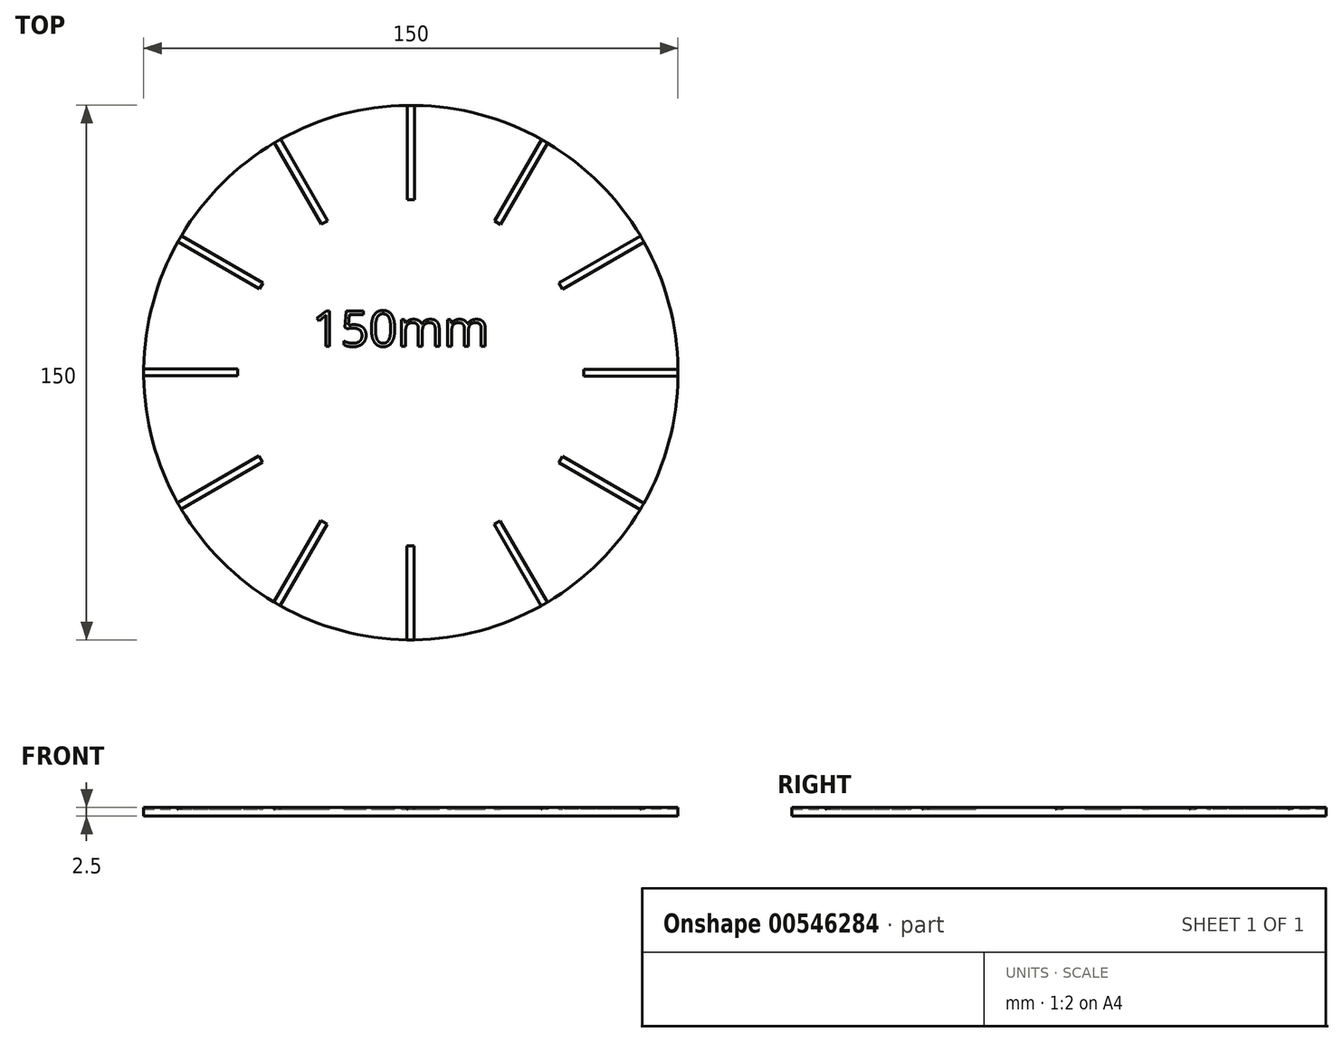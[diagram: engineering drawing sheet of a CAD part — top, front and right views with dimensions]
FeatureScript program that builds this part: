
annotation { "Feature Type Name" : "Feature", "Feature Type Description" : "" }
export const myFeature = defineFeature(function(context is Context, id is Id, definition is map)
    precondition{}
    {
        {
            var Q0;
            Q0=qCreatedBy(makeId("Top.planeOp"),FACE);
            var sketch = newSketch(context, id + "F0", { "sketchPlane" : qUnion([Q0])});
            skCircle(sketch, "E0", {"center": v(0, 0) * mm, "radius": 75 * mm});
            skSolve(sketch);
        }
        {
            var Q0;
            Q0=qSketchRegion(id+"F0",true);
            extrude(context, id + "F1", {"entities" : qUnion([Q0]), "depth" : 2.5 * mm, "offsetDistance" : 25 * mm});
        }
        {
            var Q0;
            Q0=makeQuery(id+"F1.opExtrude","CAP_FACE",FACE,{"disambiguationData":[OSD([sQuery(id+"F0.wireOp",EDGE,"E0")])],"isStart":false});
            var sketch = newSketch(context, id + "F2", { "sketchPlane" : qUnion([Q0])});
            skLineSegment(sketch, "E1.bottom", {"start": v(-0.94, 75) * mm, "end": v(1.06, 75) * mm});
            skLineSegment(sketch, "E1.top", {"start": v(-0.94, 48.58) * mm, "end": v(1.06, 48.58) * mm});
            skLineSegment(sketch, "E1.left", {"start": v(-0.94, 75) * mm, "end": v(-0.94, 48.58) * mm});
            skLineSegment(sketch, "E1.right", {"start": v(1.06, 75) * mm, "end": v(1.06, 48.58) * mm});
            skLineSegment(sketch, "E2.1.0", {"start": v(-38.3, 64.48) * mm, "end": v(-25.1, 41.6) * mm});
            skLineSegment(sketch, "E2.1.1", {"start": v(-36.58, 65.48) * mm, "end": v(-23.37, 42.6) * mm});
            skLineSegment(sketch, "E2.1.2", {"start": v(-25.1, 41.6) * mm, "end": v(-23.37, 42.6) * mm});
            skLineSegment(sketch, "E2.1.3", {"start": v(-38.3, 64.48) * mm, "end": v(-36.58, 65.48) * mm});
            skLineSegment(sketch, "E2.2.0", {"start": v(-65.42, 36.69) * mm, "end": v(-42.54, 23.48) * mm});
            skLineSegment(sketch, "E2.2.1", {"start": v(-64.42, 38.42) * mm, "end": v(-41.54, 25.2) * mm});
            skLineSegment(sketch, "E2.2.2", {"start": v(-42.54, 23.48) * mm, "end": v(-41.54, 25.2) * mm});
            skLineSegment(sketch, "E2.2.3", {"start": v(-65.42, 36.69) * mm, "end": v(-64.42, 38.42) * mm});
            skPoint(sketch, "E2.center", {"position": v(0, 0) * mm});
            skLineSegment(sketch, "E3.2.3.0", {"start": v(-75, -0.94) * mm, "end": v(-48.58, -0.94) * mm});
            skLineSegment(sketch, "E3.3.3.0", {"start": v(-75, 1.06) * mm, "end": v(-48.58, 1.06) * mm});
            skLineSegment(sketch, "E3.6.3.0", {"start": v(-48.58, -0.94) * mm, "end": v(-48.58, 1.06) * mm});
            skLineSegment(sketch, "E3.9.3.0", {"start": v(-75, -0.94) * mm, "end": v(-75, 1.06) * mm});
            skLineSegment(sketch, "E3.2.4.0", {"start": v(-64.48, -38.3) * mm, "end": v(-41.6, -25.1) * mm});
            skLineSegment(sketch, "E3.3.4.0", {"start": v(-65.48, -36.58) * mm, "end": v(-42.6, -23.37) * mm});
            skLineSegment(sketch, "E3.6.4.0", {"start": v(-41.6, -25.1) * mm, "end": v(-42.6, -23.37) * mm});
            skLineSegment(sketch, "E3.9.4.0", {"start": v(-64.48, -38.3) * mm, "end": v(-65.48, -36.58) * mm});
            skLineSegment(sketch, "E3.2.5.0", {"start": v(-36.69, -65.42) * mm, "end": v(-23.48, -42.54) * mm});
            skLineSegment(sketch, "E3.3.5.0", {"start": v(-38.42, -64.42) * mm, "end": v(-25.2, -41.54) * mm});
            skLineSegment(sketch, "E3.6.5.0", {"start": v(-23.48, -42.54) * mm, "end": v(-25.2, -41.54) * mm});
            skLineSegment(sketch, "E3.9.5.0", {"start": v(-36.69, -65.42) * mm, "end": v(-38.42, -64.42) * mm});
            skLineSegment(sketch, "E3.2.6.0", {"start": v(0.94, -75) * mm, "end": v(0.94, -48.58) * mm});
            skLineSegment(sketch, "E3.3.6.0", {"start": v(-1.06, -75) * mm, "end": v(-1.06, -48.58) * mm});
            skLineSegment(sketch, "E3.6.6.0", {"start": v(0.94, -48.58) * mm, "end": v(-1.06, -48.58) * mm});
            skLineSegment(sketch, "E3.9.6.0", {"start": v(0.94, -75) * mm, "end": v(-1.06, -75) * mm});
            skLineSegment(sketch, "E3.2.7.0", {"start": v(38.3, -64.48) * mm, "end": v(25.1, -41.6) * mm});
            skLineSegment(sketch, "E3.3.7.0", {"start": v(36.58, -65.48) * mm, "end": v(23.37, -42.6) * mm});
            skLineSegment(sketch, "E3.6.7.0", {"start": v(25.1, -41.6) * mm, "end": v(23.37, -42.6) * mm});
            skLineSegment(sketch, "E3.9.7.0", {"start": v(38.3, -64.48) * mm, "end": v(36.58, -65.48) * mm});
            skLineSegment(sketch, "E3.2.8.0", {"start": v(65.42, -36.69) * mm, "end": v(42.54, -23.48) * mm});
            skLineSegment(sketch, "E3.3.8.0", {"start": v(64.42, -38.42) * mm, "end": v(41.54, -25.2) * mm});
            skLineSegment(sketch, "E3.6.8.0", {"start": v(42.54, -23.48) * mm, "end": v(41.54, -25.2) * mm});
            skLineSegment(sketch, "E3.9.8.0", {"start": v(65.42, -36.69) * mm, "end": v(64.42, -38.42) * mm});
            skLineSegment(sketch, "E3.2.9.0", {"start": v(75, 0.94) * mm, "end": v(48.58, 0.94) * mm});
            skLineSegment(sketch, "E3.3.9.0", {"start": v(75, -1.06) * mm, "end": v(48.58, -1.06) * mm});
            skLineSegment(sketch, "E3.6.9.0", {"start": v(48.58, 0.94) * mm, "end": v(48.58, -1.06) * mm});
            skLineSegment(sketch, "E3.9.9.0", {"start": v(75, 0.94) * mm, "end": v(75, -1.06) * mm});
            skLineSegment(sketch, "E3.2.10.0", {"start": v(64.48, 38.3) * mm, "end": v(41.6, 25.1) * mm});
            skLineSegment(sketch, "E3.3.10.0", {"start": v(65.48, 36.58) * mm, "end": v(42.6, 23.37) * mm});
            skLineSegment(sketch, "E3.6.10.0", {"start": v(41.6, 25.1) * mm, "end": v(42.6, 23.37) * mm});
            skLineSegment(sketch, "E3.9.10.0", {"start": v(64.48, 38.3) * mm, "end": v(65.48, 36.58) * mm});
            skLineSegment(sketch, "E3.2.11.0", {"start": v(36.69, 65.42) * mm, "end": v(23.48, 42.54) * mm});
            skLineSegment(sketch, "E3.3.11.0", {"start": v(38.42, 64.42) * mm, "end": v(25.2, 41.54) * mm});
            skLineSegment(sketch, "E3.6.11.0", {"start": v(23.48, 42.54) * mm, "end": v(25.2, 41.54) * mm});
            skLineSegment(sketch, "E3.9.11.0", {"start": v(36.69, 65.42) * mm, "end": v(38.42, 64.42) * mm});
            skSolve(sketch);
        }
        {
            var Q0;
            Q0=qSketchRegion(id+"F2",true);
            extrude(context, id + "F3", {"entities" : qUnion([Q0]), "operationType" : NewBodyOperationType.REMOVE, "oppositeDirection" : true, "depth" : .5 * mm, "offsetDistance" : 25 * mm});
        }
        {
            var Q0;
            Q0=makeQuery(id+"F1.opExtrude","CAP_FACE",FACE,{"disambiguationData":[OSD([sQuery(id+"F0.wireOp",EDGE,"E0")])],"isStart":false});
            var sketch = newSketch(context, id + "F4", { "sketchPlane" : qUnion([Q0])});
            skText(sketch, "E4", { "text": "150mm\n", "fontName": "OpenSans-Regular.ttf"});
            const initialGuessF4  = {"E4": [-0.02765, 0.00738, 1, 0, 0.01]};
            skSetInitialGuess(sketch, initialGuessF4);
            skSolve(sketch);
        }
        {
            var Q0;
            Q0=qSketchRegion(id+"F4",true);
            extrude(context, id + "F5", {"entities" : qUnion([Q0]), "operationType" : NewBodyOperationType.REMOVE, "oppositeDirection" : true, "depth" : .5 * mm, "offsetDistance" : 25 * mm});
        }
    });
